SOLIDWORKS PART (.sldprt)
format: sldprt  version: not decoded by parser v0  size: 656,896 bytes
history: native  units: mm
features: sketch x10, extrude x7, plane x4, cut_extrude x3, mirror x2, material x1 (+8 scaffold rows collapsed)
feature tree (35):
  scaffold x8  (default folders/planes/origin — collapsed)
  material  "Material <not specified>"
  plane  "Alzado"
  plane  "Planta"
  plane  "Vista lateral"
  sketch  "Croquis1"  dims[c1.D3=3.2mm c1.D6=3.2mm c1.D10=3.2mm c1.D13=3.2mm c1.D16=3.2mm c1.D17=3.2mm c1.D22=3.2mm c1.D25=3.2mm c1.D28=3.2mm c1.D29=3.2mm c1.D1=146.04mm c1.D2=101.0mm c2.D3=~66.049961mm c2.D4=8.99mm c2.D5=2.7mm c2.D7=1.64mm c2.D8=12.42mm c2.D9=3.2mm c2.D11=87.15mm c2.D12=9.88mm c2.D14=2.68mm c2.D15=142.8mm c2.D18=1.93mm c2.D19=1.64mm c2.D20=86.08mm c2.D21=93.28mm c2.D23=8.89mm c2.D24=97.82mm c2.D26=142.8mm c2.D27=97.8mm c2.D30=87.36mm c2.D31=87.63mm c2.D32=89.89mm c2.D33=90.84mm]
  extrude  "Extruir1"  Depth=1.6mm
  sketch  "Croquis2"  dims[D1=6.5mm D2=6.5mm D3=6.5mm D4=6.5mm D5=6.5mm D6=6.5mm D7=6.5mm D8=6.5mm D9=6.5mm D10=6.5mm]
  cut_extrude  "Cortar-Extruir1"  Depth=0.2mm
  plane  "Plano1"
  mirror  "Simetría1"
  sketch  "Croquis3"  dims[D1=0.0mm D2=0.0mm D3=0.0mm D4=0.0mm D5=0.0mm D6=0.0mm D7=0.0mm D8=0.0mm D9=0.0mm]
  extrude  "Extruir2"  Depth=0.2mm
  mirror  "Simetría2"
  sketch  "Croquis4"  dims[D1=14.0mm D2=16.6mm D3=19.3mm D4=20.0mm]
  extrude  "Extruir3"  Depth=1mm
  sketch  "Croquis5"  dims[D1=5.0mm D2=14.0mm D3=14.0mm D4=14.0mm D5=7.5mm D6=26.0mm]
  extrude  "Extruir4"  Depth=1.5mm
  sketch  "Croquis6"  dims[D1=7.5mm D2=15.0mm D3=26.8mm D4=76.0mm]
  extrude  "Extruir5"  Depth=2.5mm
  sketch  "Croquis7"  dims[D1=2.0mm D2=2.0mm D3=40.16mm D4=38.01mm D5=37.54mm]
  cut_extrude  "Cortar-Extruir2"  Depth=0.2mm
  sketch  "Croquis8"  dims[D1=8.7mm D2=8.7mm D3=3.5mm D4=3.5mm D5=12.5mm D6=3.5mm D7=16.5mm D8=17.5mm]
  extrude  "Extruir6"  Depth=2mm
  sketch  "Croquis9"  dims[D1=9.0mm D2=47.0mm D3=16.0mm]
  extrude  "Extruir7"  Depth=4.2mm
  sketch  "Croquis10"
  cut_extrude  "Cortar-Extruir3"  Depth=1.2mm
decode coverage: 19 of 22 modeling features carry decoded parameters
note: ~ marks probable driven/reference dimensions
note: suppression state not decoded; provenance and decode notes live in map.json
